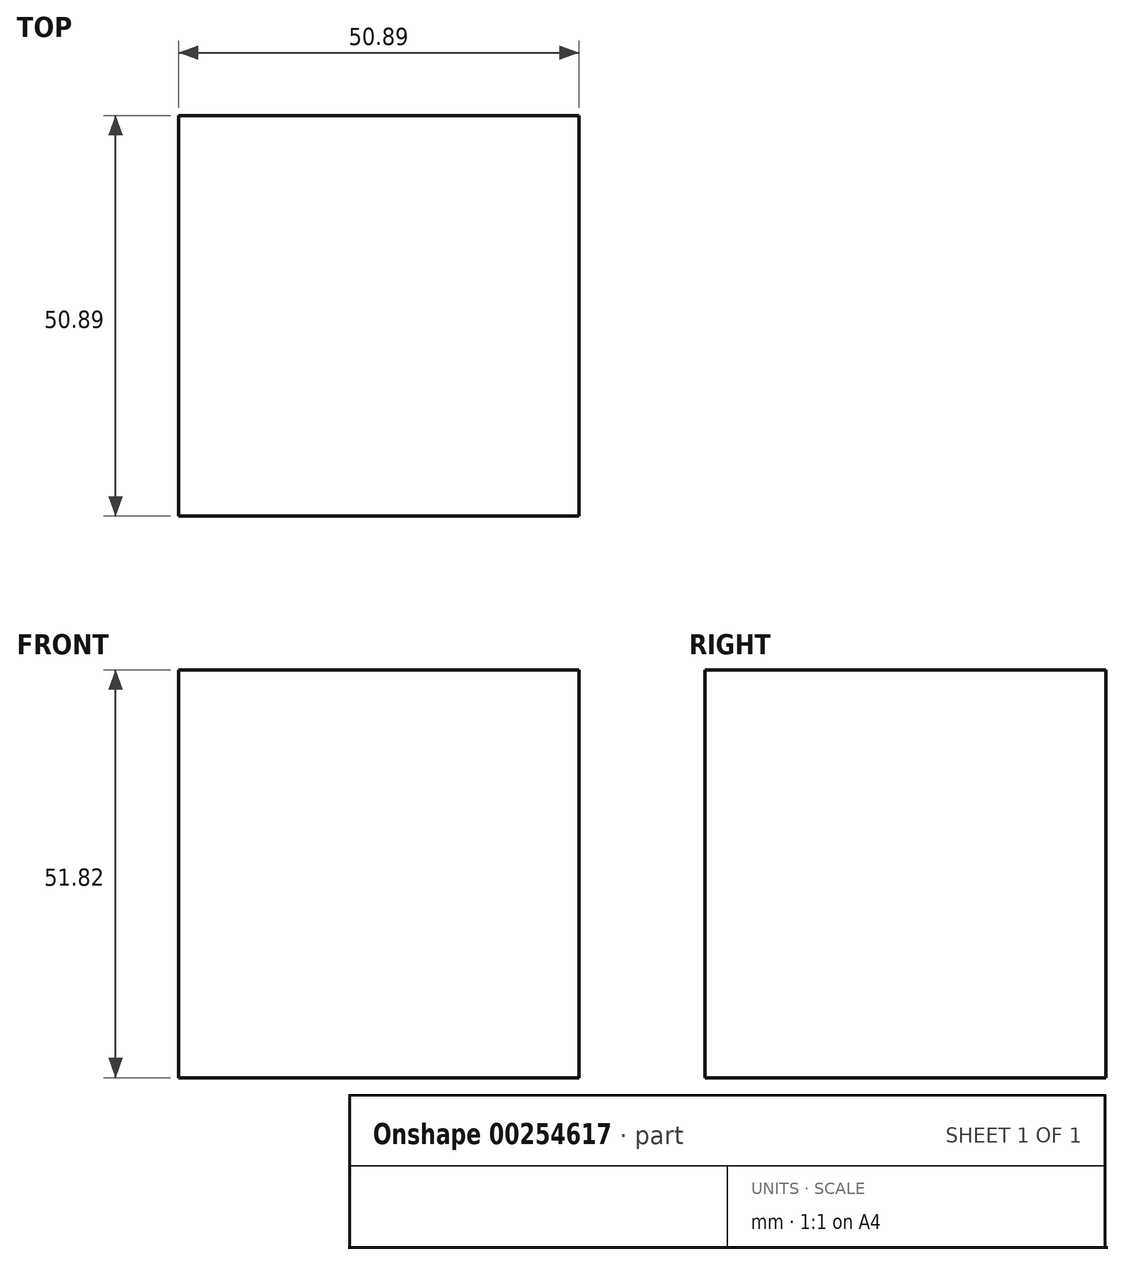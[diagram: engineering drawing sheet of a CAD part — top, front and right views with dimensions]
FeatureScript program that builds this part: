
annotation { "Feature Type Name" : "Feature", "Feature Type Description" : "" }
export const myFeature = defineFeature(function(context is Context, id is Id, definition is map)
    precondition{}
    {
        {
            var Q0;
            Q0=qCreatedBy(makeId("Top.planeOp"),FACE);
            var sketch = newSketch(context, id + "F0", { "sketchPlane" : qUnion([Q0])});
            skLineSegment(sketch, "E0", {"start": v(0, 0) * mm, "end": v(50.9, 0) * mm});
            skLineSegment(sketch, "E1", {"start": v(50.9, 0) * mm, "end": v(50.9, 50.9) * mm});
            skLineSegment(sketch, "E2", {"start": v(50.9, 50.9) * mm, "end": v(0, 50.9) * mm});
            skLineSegment(sketch, "E3", {"start": v(0, 50.9) * mm, "end": v(0, 0) * mm});
            skSolve(sketch);
        }
        {
            var Q0;
            Q0=makeQuery(id+"F0.imprint","IMPRINT",FACE,{"disambiguationData":[TD([[makeQuery(id+"F0.imprint","IMPRINT",EDGE,{"derivedFrom":sQuery(id+"F0.wireOp",EDGE,"E0")}),1.0]])]});
            extrude(context, id + "F1", {"entities" : qUnion([Q0]), "depth" : 51.82 * mm});
        }
    });
